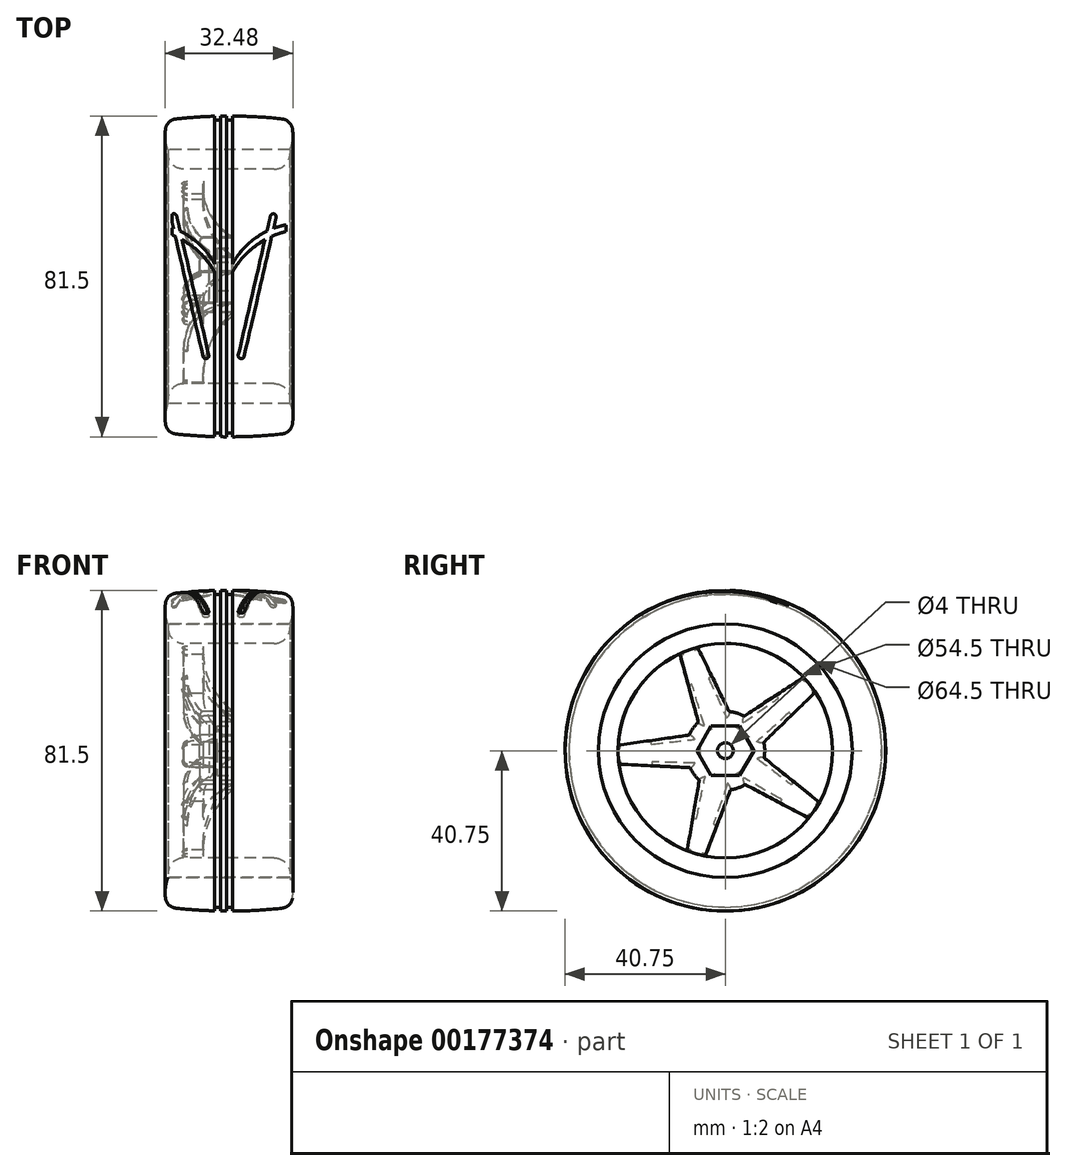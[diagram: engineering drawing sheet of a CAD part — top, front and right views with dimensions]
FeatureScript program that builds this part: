
annotation { "Feature Type Name" : "Feature", "Feature Type Description" : "" }
export const myFeature = defineFeature(function(context is Context, id is Id, definition is map)
    precondition{}
    {
        {
            var Q0;
            Q0=qCreatedBy(makeId("Front.planeOp"),FACE);
            var sketch = newSketch(context, id + "F0", { "sketchPlane" : qUnion([Q0])});
            skLineSegment(sketch, "E0", {"start": v(0, 0) * mm, "end": v(0, 27.25) * mm, "construction": true});
            skLineSegment(sketch, "E1", {"start": v(0, 27.25) * mm, "end": v(18.55, 27.25) * mm, "construction": true});
            skLineSegment(sketch, "E2", {"start": v(18.55, 27.25) * mm, "end": v(18.55, 32.25) * mm, "construction": true});
            skLineSegment(sketch, "E3", {"start": v(18.55, 32.25) * mm, "end": v(-12.45, 32.25) * mm, "construction": true});
            skLineSegment(sketch, "E4", {"start": v(-12.45, 32.25) * mm, "end": v(-12.45, 27.25) * mm, "construction": true});
            skLineSegment(sketch, "E5", {"start": v(-12.45, 27.25) * mm, "end": v(-1.95, 27.25) * mm, "construction": true});
            skLineSegment(sketch, "E6", {"start": v(-1.95, 27.25) * mm, "end": v(-1.95, 0) * mm, "construction": true});
            skLineSegment(sketch, "E7", {"start": v(-1.95, 0) * mm, "end": v(0, 0) * mm, "construction": true});
            skSolve(sketch);
        }
        {
            var Q0;
            Q0=qCreatedBy(makeId("Front.planeOp"),FACE);
            var sketch = newSketch(context, id + "F1", { "sketchPlane" : qUnion([Q0])});
            skLineSegment(sketch, "E8", {"start": v(-20, 0) * mm, "end": v(20, 0) * mm, "construction": true});
            skLineSegment(sketch, "E9", {"start": v(-1.95, 2) * mm, "end": v(0, 2) * mm});
            skLineSegment(sketch, "E10", {"start": v(0, 2) * mm, "end": v(0, 6.5) * mm, "construction": true});
            skLineSegment(sketch, "E11", {"start": v(0, 6.5) * mm, "end": v(-1.95, 6.5) * mm, "construction": true});
            skLineSegment(sketch, "E12", {"start": v(-1.95, 6.5) * mm, "end": v(-1.95, 2) * mm});
            skLineSegment(sketch, "E13", {"start": v(-8.45, 27.25) * mm, "end": v(-8.45, 18.86) * mm});
            skArc(sketch, "E14", {"start": v(-8.45, 18.86) * mm, "mid": v(-6.73, 11.88) * mm, "end": v(-1.95, 6.5) * mm});
            skArc(sketch, "E15", {"start": v(-12.45, 31.25) * mm, "mid": v(-11.28, 28.42) * mm, "end": v(-8.45, 27.25) * mm});
            skLineSegment(sketch, "E16", {"start": v(-12.45, 31.25) * mm, "end": v(-12.45, 32.25) * mm});
            skLineSegment(sketch, "E17", {"start": v(-12.45, 32.25) * mm, "end": v(18.55, 32.25) * mm});
            skLineSegment(sketch, "E18", {"start": v(18.55, 32.25) * mm, "end": v(18.55, 31.25) * mm});
            skLineSegment(sketch, "E19", {"start": v(14.55, 27.25) * mm, "end": v(-3.45, 27.25) * mm});
            skArc(sketch, "E20", {"start": v(-3.45, 27.25) * mm, "mid": v(-1.97, 17.9) * mm, "end": v(3.64, 10.3) * mm});
            skPoint(sketch, "E21.visualSharp", {"position": v(18.55, 27.25) * mm});
            skArc(sketch, "E21.filletArc", {"start": v(14.55, 27.25) * mm, "mid": v(17.38, 28.42) * mm, "end": v(18.55, 31.25) * mm});
            skLineSegment(sketch, "E22", {"start": v(4, 9.53) * mm, "end": v(4, 3) * mm});
            skLineSegment(sketch, "E23", {"start": v(4, 3) * mm, "end": v(0, 3) * mm});
            skLineSegment(sketch, "E24", {"start": v(0, 3) * mm, "end": v(0, 2) * mm});
            skPoint(sketch, "E25.visualSharp", {"position": v(4, 10) * mm});
            skArc(sketch, "E25.filletArc", {"start": v(4, 9.53) * mm, "mid": v(3.9, 9.95) * mm, "end": v(3.64, 10.3) * mm});
            skSolve(sketch);
        }
        {
            var Q0;
            Q0 = qSketchRegion(id + "F1", true);
            var Q1;
            Q1=sQuery(id+"F1.wireOp",EDGE,"E8");
            revolve(context, id + "F2", {"surfaceOperationType" : NewSurfaceOperationType.NEW, "entities" : qUnion([Q0]), "axis" : qUnion([Q1]), "revolveType" : RevolveType.FULL});
        }
        {
            var Q0;
            Q0=makeQuery(id+"F2.opRevolve","SWEPT_FACE",FACE,{"disambiguationData":[OSD([sQuery(id+"F1.wireOp",EDGE,"E22")])]});
            var sketch = newSketch(context, id + "F3", { "sketchPlane" : qUnion([Q0])});
            skCircle(sketch, "E26.cCircle", {"center": v(0, 0) * mm, "radius": 6.25 * mm, "construction": true});
            skLineSegment(sketch, "E26.0", {"start": v(-3.6, 6.25) * mm, "end": v(3.6, 6.25) * mm});
            skLineSegment(sketch, "E26.1", {"start": v(3.6, 6.25) * mm, "end": v(7.22, 0) * mm});
            skLineSegment(sketch, "E26.2", {"start": v(7.22, 0) * mm, "end": v(3.6, -6.25) * mm});
            skLineSegment(sketch, "E26.3", {"start": v(3.6, -6.25) * mm, "end": v(-3.6, -6.25) * mm});
            skLineSegment(sketch, "E26.4", {"start": v(-3.6, -6.25) * mm, "end": v(-7.22, 0) * mm});
            skLineSegment(sketch, "E26.5", {"start": v(-7.22, 0) * mm, "end": v(-3.6, 6.25) * mm});
            skPoint(sketch, "E26.0.midPoint", {"position": v(0, 6.25) * mm});
            skSolve(sketch);
        }
        {
            var Q0;
            Q0 = qSketchRegion(id + "F3", true);
            var Q1;
            Q1=makeQuery(id+"F2.opRevolve","SWEPT_FACE",FACE,{"disambiguationData":[OSD([sQuery(id+"F1.wireOp",EDGE,"E24")])]});
            extrude(context, id + "F4", {"entities" : qUnion([Q0]), "operationType" : NewBodyOperationType.REMOVE, "endBound" : BoundingType.UP_TO_SURFACE, "oppositeDirection" : true, "depth" : 25 * mm, "endBoundEntityFace" : qUnion([Q1]), "offsetDistance" : 25 * mm});
        }
        {
            var Q0;
            Q0=makeQuery(id+"F2.opRevolve","SWEPT_FACE",FACE,{"disambiguationData":[OSD([sQuery(id+"F1.wireOp",EDGE,"E16")])]});
            var sketch = newSketch(context, id + "F5", { "sketchPlane" : qUnion([Q0])});
            skLineSegment(sketch, "E27", {"start": v(11.62, 24.65) * mm, "end": v(6.88, 7.26) * mm});
            skArc(sketch, "E28", {"start": v(9.17, 3.98) * mm, "mid": v(8.2, 5.74) * mm, "end": v(6.88, 7.26) * mm});
            skLineSegment(sketch, "E29", {"start": v(9.17, 3.98) * mm, "end": v(27.21, 1.4) * mm});
            skArc(sketch, "E30", {"start": v(27.21, 1.4) * mm, "mid": v(22.63, 15.18) * mm, "end": v(11.62, 24.65) * mm});
            skLineSegment(sketch, "E31", {"start": v(0, 0) * mm, "end": v(22.32, 15.63) * mm, "construction": true});
            skLineSegment(sketch, "E32.1.0", {"start": v(-19.85, 18.66) * mm, "end": v(-4.78, 8.79) * mm});
            skArc(sketch, "E32.1.1", {"start": v(7.08, 26.31) * mm, "mid": v(-7.44, 26.21) * mm, "end": v(-19.85, 18.66) * mm});
            skLineSegment(sketch, "E32.1.2", {"start": v(-0.95, 9.95) * mm, "end": v(7.08, 26.31) * mm});
            skArc(sketch, "E32.1.3", {"start": v(-0.95, 9.95) * mm, "mid": v(-2.92, 9.56) * mm, "end": v(-4.78, 8.79) * mm});
            skLineSegment(sketch, "E32.2.0", {"start": v(-23.89, -13.12) * mm, "end": v(-9.83, -1.83) * mm});
            skArc(sketch, "E32.2.1", {"start": v(-22.84, 14.87) * mm, "mid": v(-27.23, 1.02) * mm, "end": v(-23.89, -13.12) * mm});
            skLineSegment(sketch, "E32.2.2", {"start": v(-9.76, 2.17) * mm, "end": v(-22.84, 14.87) * mm});
            skArc(sketch, "E32.2.3", {"start": v(-9.76, 2.17) * mm, "mid": v(-10, 0.17) * mm, "end": v(-9.83, -1.83) * mm});
            skLineSegment(sketch, "E32.3.0", {"start": v(5.1, -26.77) * mm, "end": v(-1.3, -9.92) * mm});
            skArc(sketch, "E32.3.1", {"start": v(-21.2, -17.13) * mm, "mid": v(-9.38, -25.58) * mm, "end": v(5.1, -26.77) * mm});
            skLineSegment(sketch, "E32.3.2", {"start": v(-5.08, -8.61) * mm, "end": v(-21.2, -17.13) * mm});
            skArc(sketch, "E32.3.3", {"start": v(-5.08, -8.61) * mm, "mid": v(-3.26, -9.46) * mm, "end": v(-1.3, -9.92) * mm});
            skLineSegment(sketch, "E32.4.0", {"start": v(27.03, -3.43) * mm, "end": v(9.03, -4.3) * mm});
            skArc(sketch, "E32.4.1", {"start": v(9.74, -25.45) * mm, "mid": v(21.43, -16.83) * mm, "end": v(27.03, -3.43) * mm});
            skLineSegment(sketch, "E32.4.2", {"start": v(6.62, -7.5) * mm, "end": v(9.74, -25.45) * mm});
            skArc(sketch, "E32.4.3", {"start": v(6.62, -7.5) * mm, "mid": v(7.99, -6.02) * mm, "end": v(9.03, -4.3) * mm});
            skSolve(sketch);
        }
        {
            var Q0;
            Q0 = qSketchRegion(id + "F5", true);
            extrude(context, id + "F6", {"entities" : qUnion([Q0]), "operationType" : NewBodyOperationType.REMOVE, "endBound" : BoundingType.THROUGH_ALL, "oppositeDirection" : true, "depth" : 25 * mm, "offsetDistance" : 25 * mm});
        }
        {
            var Q0;
            Q0=makeQuery(id+"F6.boolean.opBoolean","INTERSECT",EDGE,{"derivedFrom":[makeQuery(id+"F2.opRevolve","SWEPT_FACE",FACE,{"disambiguationData":[OSD([sQuery(id+"F1.wireOp",EDGE,"E14")])]}),makeQuery(id+"F6.opExtrude","SWEPT_FACE",FACE,{"disambiguationData":[OSD([sQuery(id+"F5.wireOp",EDGE,"E32.2.0")])]})]});
            var Q1;
            Q1=makeQuery(id+"F6.boolean.opBoolean","INTERSECT",EDGE,{"derivedFrom":[makeQuery(id+"F2.opRevolve","SWEPT_FACE",FACE,{"disambiguationData":[OSD([sQuery(id+"F1.wireOp",EDGE,"E13")])]}),makeQuery(id+"F6.opExtrude","SWEPT_FACE",FACE,{"disambiguationData":[OSD([sQuery(id+"F5.wireOp",EDGE,"E32.3.2")])]})]});
            var Q2;
            Q2=makeQuery(id+"F6.boolean.opBoolean","INTERSECT",EDGE,{"derivedFrom":[makeQuery(id+"F2.opRevolve","SWEPT_FACE",FACE,{"disambiguationData":[OSD([sQuery(id+"F1.wireOp",EDGE,"E14")])]}),makeQuery(id+"F6.opExtrude","SWEPT_FACE",FACE,{"disambiguationData":[OSD([sQuery(id+"F5.wireOp",EDGE,"E32.3.3")])]})]});
            var Q3;
            Q3=makeQuery(id+"F6.boolean.opBoolean","INTERSECT",EDGE,{"derivedFrom":[makeQuery(id+"F2.opRevolve","SWEPT_FACE",FACE,{"disambiguationData":[OSD([sQuery(id+"F1.wireOp",EDGE,"E14")])]}),makeQuery(id+"F6.opExtrude","SWEPT_FACE",FACE,{"disambiguationData":[OSD([sQuery(id+"F5.wireOp",EDGE,"E32.2.3")])]})]});
            var Q4;
            Q4=makeQuery(id+"F6.boolean.opBoolean","INTERSECT",EDGE,{"derivedFrom":[makeQuery(id+"F2.opRevolve","SWEPT_FACE",FACE,{"disambiguationData":[OSD([sQuery(id+"F1.wireOp",EDGE,"E14")])]}),makeQuery(id+"F6.opExtrude","SWEPT_FACE",FACE,{"disambiguationData":[OSD([sQuery(id+"F5.wireOp",EDGE,"E32.2.2")])]})]});
            var Q5;
            Q5=makeQuery(id+"F6.boolean.opBoolean","INTERSECT",EDGE,{"derivedFrom":[makeQuery(id+"F2.opRevolve","SWEPT_FACE",FACE,{"disambiguationData":[OSD([sQuery(id+"F1.wireOp",EDGE,"E14")])]}),makeQuery(id+"F6.opExtrude","SWEPT_FACE",FACE,{"disambiguationData":[OSD([sQuery(id+"F5.wireOp",EDGE,"E32.1.3")])]})]});
            var Q6;
            Q6=makeQuery(id+"F6.boolean.opBoolean","INTERSECT",EDGE,{"derivedFrom":[makeQuery(id+"F2.opRevolve","SWEPT_FACE",FACE,{"disambiguationData":[OSD([sQuery(id+"F1.wireOp",EDGE,"E14")])]}),makeQuery(id+"F6.opExtrude","SWEPT_FACE",FACE,{"disambiguationData":[OSD([sQuery(id+"F5.wireOp",EDGE,"E32.1.0")])]})]});
            var Q7;
            Q7=makeQuery(id+"F6.boolean.opBoolean","INTERSECT",EDGE,{"derivedFrom":[makeQuery(id+"F2.opRevolve","SWEPT_FACE",FACE,{"disambiguationData":[OSD([sQuery(id+"F1.wireOp",EDGE,"E14")])]}),makeQuery(id+"F6.opExtrude","SWEPT_FACE",FACE,{"disambiguationData":[OSD([sQuery(id+"F5.wireOp",EDGE,"E32.3.0")])]})]});
            var Q8;
            Q8=makeQuery(id+"F6.boolean.opBoolean","INTERSECT",EDGE,{"derivedFrom":[makeQuery(id+"F2.opRevolve","SWEPT_FACE",FACE,{"disambiguationData":[OSD([sQuery(id+"F1.wireOp",EDGE,"E14")])]}),makeQuery(id+"F6.opExtrude","SWEPT_FACE",FACE,{"disambiguationData":[OSD([sQuery(id+"F5.wireOp",EDGE,"E32.4.2")])]})]});
            var Q9;
            Q9=makeQuery(id+"F6.boolean.opBoolean","INTERSECT",EDGE,{"derivedFrom":[makeQuery(id+"F2.opRevolve","SWEPT_FACE",FACE,{"disambiguationData":[OSD([sQuery(id+"F1.wireOp",EDGE,"E14")])]}),makeQuery(id+"F6.opExtrude","SWEPT_FACE",FACE,{"disambiguationData":[OSD([sQuery(id+"F5.wireOp",EDGE,"E32.4.3")])]})]});
            var Q10;
            Q10=makeQuery(id+"F6.boolean.opBoolean","INTERSECT",EDGE,{"derivedFrom":[makeQuery(id+"F2.opRevolve","SWEPT_FACE",FACE,{"disambiguationData":[OSD([sQuery(id+"F1.wireOp",EDGE,"E14")])]}),makeQuery(id+"F6.opExtrude","SWEPT_FACE",FACE,{"disambiguationData":[OSD([sQuery(id+"F5.wireOp",EDGE,"E32.4.0")])]})]});
            var Q11;
            Q11=makeQuery(id+"F6.boolean.opBoolean","INTERSECT",EDGE,{"derivedFrom":[makeQuery(id+"F2.opRevolve","SWEPT_FACE",FACE,{"disambiguationData":[OSD([sQuery(id+"F1.wireOp",EDGE,"E14")])]}),makeQuery(id+"F6.opExtrude","SWEPT_FACE",FACE,{"disambiguationData":[OSD([sQuery(id+"F5.wireOp",EDGE,"E29")])]})]});
            var Q12;
            Q12=makeQuery(id+"F6.boolean.opBoolean","INTERSECT",EDGE,{"derivedFrom":[makeQuery(id+"F2.opRevolve","SWEPT_FACE",FACE,{"disambiguationData":[OSD([sQuery(id+"F1.wireOp",EDGE,"E14")])]}),makeQuery(id+"F6.opExtrude","SWEPT_FACE",FACE,{"disambiguationData":[OSD([sQuery(id+"F5.wireOp",EDGE,"E28")])]})]});
            var Q13;
            Q13=makeQuery(id+"F6.boolean.opBoolean","INTERSECT",EDGE,{"derivedFrom":[makeQuery(id+"F2.opRevolve","SWEPT_FACE",FACE,{"disambiguationData":[OSD([sQuery(id+"F1.wireOp",EDGE,"E14")])]}),makeQuery(id+"F6.opExtrude","SWEPT_FACE",FACE,{"disambiguationData":[OSD([sQuery(id+"F5.wireOp",EDGE,"E27")])]})]});
            var Q14;
            Q14=makeQuery(id+"F6.boolean.opBoolean","INTERSECT",EDGE,{"derivedFrom":[makeQuery(id+"F2.opRevolve","SWEPT_FACE",FACE,{"disambiguationData":[OSD([sQuery(id+"F1.wireOp",EDGE,"E14")])]}),makeQuery(id+"F6.opExtrude","SWEPT_FACE",FACE,{"disambiguationData":[OSD([sQuery(id+"F5.wireOp",EDGE,"E32.1.2")])]})]});
            fillet(context, id + "F7", {"entities" : qUnion([Q0, Q1, Q2, Q3, Q4, Q5, Q6, Q7, Q8, Q9, Q10, Q11, Q12, Q13, Q14]), "radius" : 1 * mm, "tangentPropagation" : true, "allowEdgeOverflow" : false});
        }
        {
            var Q0;
            Q0=makeQuery(id+"F6.boolean.opBoolean","COPY",EDGE,{"derivedFrom":makeQuery(id+"F6.opExtrude","SWEPT_EDGE",EDGE,{"disambiguationData":[OSD([sQuery(id+"F5.wireOp",EDGE,"E32.2.1"),sQuery(id+"F5.wireOp",EDGE,"E32.2.2")])]})});
            var Q1;
            Q1=makeQuery(id+"F6.boolean.opBoolean","COPY",EDGE,{"derivedFrom":makeQuery(id+"F6.opExtrude","SWEPT_EDGE",EDGE,{"disambiguationData":[OSD([sQuery(id+"F5.wireOp",EDGE,"E27"),sQuery(id+"F5.wireOp",EDGE,"E30")])]})});
            var Q2;
            Q2=makeQuery(id+"F6.boolean.opBoolean","COPY",EDGE,{"derivedFrom":makeQuery(id+"F6.opExtrude","SWEPT_EDGE",EDGE,{"disambiguationData":[OSD([sQuery(id+"F5.wireOp",EDGE,"E32.4.0"),sQuery(id+"F5.wireOp",EDGE,"E32.4.1")])]})});
            var Q3;
            Q3=makeQuery(id+"F6.boolean.opBoolean","COPY",EDGE,{"derivedFrom":makeQuery(id+"F6.opExtrude","SWEPT_EDGE",EDGE,{"disambiguationData":[OSD([sQuery(id+"F5.wireOp",EDGE,"E32.4.1"),sQuery(id+"F5.wireOp",EDGE,"E32.4.2")])]})});
            var Q4;
            Q4=makeQuery(id+"F6.boolean.opBoolean","COPY",EDGE,{"derivedFrom":makeQuery(id+"F6.opExtrude","SWEPT_EDGE",EDGE,{"disambiguationData":[OSD([sQuery(id+"F5.wireOp",EDGE,"E32.2.0"),sQuery(id+"F5.wireOp",EDGE,"E32.2.1")])]})});
            fillet(context, id + "F8", {"entities" : qUnion([Q0, Q1, Q2, Q3, Q4]), "radius" : 0.5 * mm, "tangentPropagation" : true, "allowEdgeOverflow" : false});
        }
        {
            var Q0;
            Q0=qCreatedBy(makeId("Front.planeOp"),FACE);
            var sketch = newSketch(context, id + "F9", { "sketchPlane" : qUnion([Q0])});
            skLineSegment(sketch, "E33", {"start": v(39.81, 0) * mm, "end": v(-23.66, 0) * mm, "construction": true});
            skArc(sketch, "E34", {"start": v(16.54, 40.02) * mm, "mid": v(3.05, 40.75) * mm, "end": v(-10.44, 40.02) * mm});
            skArc(sketch, "E35", {"start": v(-13.08, 37.48) * mm, "mid": v(-13.11, 34.82) * mm, "end": v(-12.45, 32.25) * mm});
            skArc(sketch, "E36", {"start": v(18.55, 32.25) * mm, "mid": v(19.21, 34.82) * mm, "end": v(19.18, 37.48) * mm});
            skLineSegment(sketch, "E37", {"start": v(18.55, 32.25) * mm, "end": v(-12.45, 32.25) * mm});
            skPoint(sketch, "E38.visualSharp", {"position": v(18.55, 39.79) * mm});
            skArc(sketch, "E38.filletArc", {"start": v(19.18, 37.48) * mm, "mid": v(18.3, 39.2) * mm, "end": v(16.54, 40.02) * mm});
            skPoint(sketch, "E39.visualSharp", {"position": v(-12.45, 39.79) * mm});
            skArc(sketch, "E39.filletArc", {"start": v(-10.44, 40.02) * mm, "mid": v(-12.2, 39.2) * mm, "end": v(-13.08, 37.48) * mm});
            skSolve(sketch);
        }
        {
            var Q0;
            Q0 = qSketchRegion(id + "F9", true);
            var Q1;
            Q1=sQuery(id+"F9.wireOp",EDGE,"E33");
            revolve(context, id + "F10", {"surfaceOperationType" : NewSurfaceOperationType.NEW, "entities" : qUnion([Q0]), "axis" : qUnion([Q1]), "revolveType" : RevolveType.FULL});
        }
        {
            var Q0;
            Q0=qCreatedBy(makeId("Front.planeOp"),FACE);
            var sketch = newSketch(context, id + "F11", { "sketchPlane" : qUnion([Q0])});
            skLineSegment(sketch, "E40", {"start": v(0.92, 41.75) * mm, "end": v(0.92, 39.75) * mm});
            skLineSegment(sketch, "E41", {"start": v(-0.58, 39.75) * mm, "end": v(-0.58, 41.75) * mm});
            skLineSegment(sketch, "E42", {"start": v(-0.58, 41.75) * mm, "end": v(0.92, 41.75) * mm});
            skLineSegment(sketch, "E43", {"start": v(3.92, 41.75) * mm, "end": v(3.92, 39.75) * mm});
            skLineSegment(sketch, "E44", {"start": v(2.42, 39.75) * mm, "end": v(2.42, 41.75) * mm});
            skLineSegment(sketch, "E45", {"start": v(2.42, 41.75) * mm, "end": v(3.92, 41.75) * mm});
            skLineSegment(sketch, "E46", {"start": v(3.92, 39.75) * mm, "end": v(2.42, 39.75) * mm});
            skLineSegment(sketch, "E47", {"start": v(0.92, 39.75) * mm, "end": v(-0.58, 39.75) * mm});
            skLineSegment(sketch, "E48", {"start": v(0, 0) * mm, "end": v(-18.32, 0) * mm, "construction": true});
            skSolve(sketch);
        }
        {
            var Q0;
            Q0 = qSketchRegion(id + "F11", true);
            var Q1;
            Q1=makeQuery(id+"F10.opRevolve","SWEPT_FACE",FACE,{"disambiguationData":[OSD([sQuery(id+"F9.wireOp",EDGE,"E34")])]});
            revolve(context, id + "F12", {"operationType" : NewBodyOperationType.REMOVE, "surfaceOperationType" : NewSurfaceOperationType.NEW, "entities" : qUnion([Q0]), "axis" : qUnion([Q1]), "revolveType" : RevolveType.FULL, "oppositeDirection" : true});
        }
        {
            var Q0;
            Q0=qCreatedBy(makeId("Top.planeOp"),FACE);
            cPlane(context, id + "F13", {"entities" : qUnion([Q0]), "cplaneType" : CPlaneType.OFFSET, "offset" : 42.75 * mm, "width" : 150 * mm, "height" : 150 * mm});
        }
        {
            var Q0;
            Q0=qCreatedBy(id+"F13.planeOp",FACE);
            var sketch = newSketch(context, id + "F14", { "sketchPlane" : qUnion([Q0])});
            skLineSegment(sketch, "E49", {"start": v(0, 0) * mm, "end": v(0, 2) * mm});
            skArc(sketch, "E50", {"start": v(0, 2) * mm, "mid": v(-7.37, 10.38) * mm, "end": v(-18.08, 13.5) * mm});
            skArc(sketch, "E51", {"start": v(0, 0) * mm, "mid": v(-7.42, 8.45) * mm, "end": v(-18.08, 12) * mm});
            skLineSegment(sketch, "E52", {"start": v(-18.08, 12) * mm, "end": v(-18.08, 13.5) * mm});
            skLineSegment(sketch, "E53", {"start": v(1.67, 6.52) * mm, "end": v(1.67, -6.35) * mm, "construction": true});
            skArc(sketch, "E54.MirrorCS", {"start": v(3.34, 0) * mm, "mid": v(10.75, 8.45) * mm, "end": v(21.42, 12) * mm});
            skArc(sketch, "E55.MirrorCS", {"start": v(3.34, 2) * mm, "mid": v(10.7, 10.38) * mm, "end": v(21.42, 13.5) * mm});
            skLineSegment(sketch, "E56.MirrorCS", {"start": v(21.42, 12) * mm, "end": v(21.42, 13.5) * mm});
            skLineSegment(sketch, "E57.MirrorCS", {"start": v(3.34, 0) * mm, "end": v(3.34, 2) * mm});
            skSolve(sketch);
        }
        {
            var Q0;
            Q0 = qSketchRegion(id + "F14", true);
            var Q1;
            Q1=makeQuery(id+"F12.boolean.opBoolean","COPY",FACE,{"derivedFrom":makeQuery(id+"F12.opRevolve","SWEPT_FACE",FACE,{"disambiguationData":[OSD([sQuery(id+"F11.wireOp",EDGE,"E46")])]})});
            extrude(context, id + "F15", {"entities" : qUnion([Q0]), "operationType" : NewBodyOperationType.REMOVE, "endBound" : BoundingType.UP_TO_SURFACE, "oppositeDirection" : true, "depth" : 25 * mm, "endBoundEntityFace" : qUnion([Q1]), "offsetDistance" : 25 * mm});
        }
        {
            var Q0;
            Q0=qCreatedBy(id+"F13.planeOp",FACE);
            var sketch = newSketch(context, id + "F16", { "sketchPlane" : qUnion([Q0])});
            skLineSegment(sketch, "E58", {"start": v(5.42, -20) * mm, "end": v(13.57, 15.34) * mm});
            skLineSegment(sketch, "E59", {"start": v(13.57, 15.34) * mm, "end": v(15.04, 15) * mm, "construction": true});
            skLineSegment(sketch, "E60", {"start": v(15.04, 15) * mm, "end": v(6.88, -20.34) * mm});
            skLineSegment(sketch, "E61", {"start": v(6.88, -20.34) * mm, "end": v(5.42, -20) * mm, "construction": true});
            skArc(sketch, "E62", {"start": v(15.04, 15) * mm, "mid": v(14.47, 15.9) * mm, "end": v(13.57, 15.34) * mm});
            skArc(sketch, "E63", {"start": v(5.42, -20) * mm, "mid": v(5.98, -20.9) * mm, "end": v(6.88, -20.34) * mm});
            skLineSegment(sketch, "E64", {"start": v(1.67, 11.65) * mm, "end": v(1.67, -13.65) * mm, "construction": true});
            skLineSegment(sketch, "E65.MirrorCS", {"start": v(-2.08, -20) * mm, "end": v(-10.23, 15.34) * mm});
            skLineSegment(sketch, "E66.MirrorCS", {"start": v(-11.7, 15) * mm, "end": v(-3.54, -20.34) * mm});
            skArc(sketch, "E67.MirrorCS", {"start": v(-11.7, 15) * mm, "mid": v(-11.13, 15.9) * mm, "end": v(-10.23, 15.34) * mm});
            skArc(sketch, "E68.MirrorCS", {"start": v(-2.08, -20) * mm, "mid": v(-2.64, -20.9) * mm, "end": v(-3.54, -20.34) * mm});
            skSolve(sketch);
        }
        {
            var Q0;
            Q0=makeQuery(id+"F16.imprint","IMPRINT",FACE,{"disambiguationData":[TD([[makeQuery(id+"F16.imprint","IMPRINT",EDGE,{"derivedFrom":sQuery(id+"F16.wireOp",EDGE,"E58")}),-1.0]])]});
            var Q1;
            Q1=makeQuery(id+"F16.imprint","IMPRINT",FACE,{"disambiguationData":[TD([[makeQuery(id+"F16.imprint","IMPRINT",EDGE,{"derivedFrom":sQuery(id+"F16.wireOp",EDGE,"E65.MirrorCS")}),1.0]])]});
            var Q2;
            {var subQ0=sQuery(id+"F14.wireOp",EDGE,"E57.MirrorCS");var subQ1=sQuery(id+"F14.wireOp",EDGE,"E56.MirrorCS");var subQ2=sQuery(id+"F14.wireOp",EDGE,"E55.MirrorCS");var subQ3=sQuery(id+"F14.wireOp",EDGE,"E54.MirrorCS");Q2=makeQuery(id+"FRkk9yGD8DPVHCN_2.23.F15.boolean.opBoolean","MERGE",FACE,{"derivedFrom":[makeQuery(id+"FRkk9yGD8DPVHCN_2.22.F15.boolean.opBoolean","MERGE",FACE,{"derivedFrom":[makeQuery(id+"FRkk9yGD8DPVHCN_2.21.F15.boolean.opBoolean","MERGE",FACE,{"derivedFrom":[makeQuery(id+"FRkk9yGD8DPVHCN_2.20.F15.boolean.opBoolean","MERGE",FACE,{"derivedFrom":[makeQuery(id+"FRkk9yGD8DPVHCN_2.19.F15.boolean.opBoolean","MERGE",FACE,{"derivedFrom":[makeQuery(id+"FRkk9yGD8DPVHCN_2.18.F15.boolean.opBoolean","MERGE",FACE,{"derivedFrom":[makeQuery(id+"FRkk9yGD8DPVHCN_2.17.F15.boolean.opBoolean","MERGE",FACE,{"derivedFrom":[makeQuery(id+"FRkk9yGD8DPVHCN_2.16.F15.boolean.opBoolean","MERGE",FACE,{"derivedFrom":[makeQuery(id+"FRkk9yGD8DPVHCN_2.15.F15.boolean.opBoolean","MERGE",FACE,{"derivedFrom":[makeQuery(id+"FRkk9yGD8DPVHCN_2.14.F15.boolean.opBoolean","MERGE",FACE,{"derivedFrom":[makeQuery(id+"FRkk9yGD8DPVHCN_2.13.F15.boolean.opBoolean","MERGE",FACE,{"derivedFrom":[makeQuery(id+"FRkk9yGD8DPVHCN_2.12.F15.boolean.opBoolean","MERGE",FACE,{"derivedFrom":[makeQuery(id+"FRkk9yGD8DPVHCN_2.11.F15.boolean.opBoolean","MERGE",FACE,{"derivedFrom":[makeQuery(id+"FRkk9yGD8DPVHCN_2.10.F15.boolean.opBoolean","MERGE",FACE,{"derivedFrom":[makeQuery(id+"FRkk9yGD8DPVHCN_2.9.F15.boolean.opBoolean","MERGE",FACE,{"derivedFrom":[makeQuery(id+"FRkk9yGD8DPVHCN_2.8.F15.boolean.opBoolean","MERGE",FACE,{"derivedFrom":[makeQuery(id+"FRkk9yGD8DPVHCN_2.7.F15.boolean.opBoolean","MERGE",FACE,{"derivedFrom":[makeQuery(id+"FRkk9yGD8DPVHCN_2.6.F15.boolean.opBoolean","MERGE",FACE,{"derivedFrom":[makeQuery(id+"FRkk9yGD8DPVHCN_2.5.F15.boolean.opBoolean","MERGE",FACE,{"derivedFrom":[makeQuery(id+"FRkk9yGD8DPVHCN_2.4.F15.boolean.opBoolean","MERGE",FACE,{"derivedFrom":[makeQuery(id+"FRkk9yGD8DPVHCN_2.3.F15.boolean.opBoolean","MERGE",FACE,{"derivedFrom":[makeQuery(id+"FRkk9yGD8DPVHCN_2.2.F15.boolean.opBoolean","MERGE",FACE,{"derivedFrom":[makeQuery(id+"FRkk9yGD8DPVHCN_2.1.F15.boolean.opBoolean","MERGE",FACE,{"derivedFrom":[makeQuery(id+"F15.boolean.opBoolean","MERGE",FACE,{"derivedFrom":[makeQuery(id+"F12.boolean.opBoolean","COPY",FACE,{"derivedFrom":makeQuery(id+"F12.opRevolve","SWEPT_FACE",FACE,{"disambiguationData":[OSD([sQuery(id+"F11.wireOp",EDGE,"E46")])]})})],"fromTools":[makeQuery(id+"F15.opExtrude","CAP_FACE",FACE,{"disambiguationData":[OSD([subQ3,subQ2,subQ1,subQ0])],"isStart":false})]})],"fromTools":[makeQuery(id+"FRkk9yGD8DPVHCN_2.1.F15.opExtrude","CAP_FACE",FACE,{"disambiguationData":[OSD([subQ3,subQ2,subQ1,subQ0])],"isStart":false})]})],"fromTools":[makeQuery(id+"FRkk9yGD8DPVHCN_2.2.F15.opExtrude","CAP_FACE",FACE,{"disambiguationData":[OSD([subQ3,subQ2,subQ1,subQ0])],"isStart":false})]})],"fromTools":[makeQuery(id+"FRkk9yGD8DPVHCN_2.3.F15.opExtrude","CAP_FACE",FACE,{"disambiguationData":[OSD([subQ3,subQ2,subQ1,subQ0])],"isStart":false})]})],"fromTools":[makeQuery(id+"FRkk9yGD8DPVHCN_2.4.F15.opExtrude","CAP_FACE",FACE,{"disambiguationData":[OSD([subQ3,subQ2,subQ1,subQ0])],"isStart":false})]})],"fromTools":[makeQuery(id+"FRkk9yGD8DPVHCN_2.5.F15.opExtrude","CAP_FACE",FACE,{"disambiguationData":[OSD([subQ3,subQ2,subQ1,subQ0])],"isStart":false})]})],"fromTools":[makeQuery(id+"FRkk9yGD8DPVHCN_2.6.F15.opExtrude","CAP_FACE",FACE,{"disambiguationData":[OSD([subQ3,subQ2,subQ1,subQ0])],"isStart":false})]})],"fromTools":[makeQuery(id+"FRkk9yGD8DPVHCN_2.7.F15.opExtrude","CAP_FACE",FACE,{"disambiguationData":[OSD([subQ3,subQ2,subQ1,subQ0])],"isStart":false})]})],"fromTools":[makeQuery(id+"FRkk9yGD8DPVHCN_2.8.F15.opExtrude","CAP_FACE",FACE,{"disambiguationData":[OSD([subQ3,subQ2,subQ1,subQ0])],"isStart":false})]})],"fromTools":[makeQuery(id+"FRkk9yGD8DPVHCN_2.9.F15.opExtrude","CAP_FACE",FACE,{"disambiguationData":[OSD([subQ3,subQ2,subQ1,subQ0])],"isStart":false})]})],"fromTools":[makeQuery(id+"FRkk9yGD8DPVHCN_2.10.F15.opExtrude","CAP_FACE",FACE,{"disambiguationData":[OSD([subQ3,subQ2,subQ1,subQ0])],"isStart":false})]})],"fromTools":[makeQuery(id+"FRkk9yGD8DPVHCN_2.11.F15.opExtrude","CAP_FACE",FACE,{"disambiguationData":[OSD([subQ3,subQ2,subQ1,subQ0])],"isStart":false})]})],"fromTools":[makeQuery(id+"FRkk9yGD8DPVHCN_2.12.F15.opExtrude","CAP_FACE",FACE,{"disambiguationData":[OSD([subQ3,subQ2,subQ1,subQ0])],"isStart":false})]})],"fromTools":[makeQuery(id+"FRkk9yGD8DPVHCN_2.13.F15.opExtrude","CAP_FACE",FACE,{"disambiguationData":[OSD([subQ3,subQ2,subQ1,subQ0])],"isStart":false})]})],"fromTools":[makeQuery(id+"FRkk9yGD8DPVHCN_2.14.F15.opExtrude","CAP_FACE",FACE,{"disambiguationData":[OSD([subQ3,subQ2,subQ1,subQ0])],"isStart":false})]})],"fromTools":[makeQuery(id+"FRkk9yGD8DPVHCN_2.15.F15.opExtrude","CAP_FACE",FACE,{"disambiguationData":[OSD([subQ3,subQ2,subQ1,subQ0])],"isStart":false})]})],"fromTools":[makeQuery(id+"FRkk9yGD8DPVHCN_2.16.F15.opExtrude","CAP_FACE",FACE,{"disambiguationData":[OSD([subQ3,subQ2,subQ1,subQ0])],"isStart":false})]})],"fromTools":[makeQuery(id+"FRkk9yGD8DPVHCN_2.17.F15.opExtrude","CAP_FACE",FACE,{"disambiguationData":[OSD([subQ3,subQ2,subQ1,subQ0])],"isStart":false})]})],"fromTools":[makeQuery(id+"FRkk9yGD8DPVHCN_2.18.F15.opExtrude","CAP_FACE",FACE,{"disambiguationData":[OSD([subQ3,subQ2,subQ1,subQ0])],"isStart":false})]})],"fromTools":[makeQuery(id+"FRkk9yGD8DPVHCN_2.19.F15.opExtrude","CAP_FACE",FACE,{"disambiguationData":[OSD([subQ3,subQ2,subQ1,subQ0])],"isStart":false})]})],"fromTools":[makeQuery(id+"FRkk9yGD8DPVHCN_2.20.F15.opExtrude","CAP_FACE",FACE,{"disambiguationData":[OSD([subQ3,subQ2,subQ1,subQ0])],"isStart":false})]})],"fromTools":[makeQuery(id+"FRkk9yGD8DPVHCN_2.21.F15.opExtrude","CAP_FACE",FACE,{"disambiguationData":[OSD([subQ3,subQ2,subQ1,subQ0])],"isStart":false})]})],"fromTools":[makeQuery(id+"FRkk9yGD8DPVHCN_2.22.F15.opExtrude","CAP_FACE",FACE,{"disambiguationData":[OSD([subQ3,subQ2,subQ1,subQ0])],"isStart":false})]})],"fromTools":[makeQuery(id+"FRkk9yGD8DPVHCN_2.23.F15.opExtrude","CAP_FACE",FACE,{"disambiguationData":[OSD([subQ3,subQ2,subQ1,subQ0])],"isStart":false})]});}
            extrude(context, id + "F17", {"entities" : qUnion([Q0, Q1]), "operationType" : NewBodyOperationType.REMOVE, "endBound" : BoundingType.UP_TO_SURFACE, "oppositeDirection" : true, "depth" : 25 * mm, "endBoundEntityFace" : qUnion([Q2]), "offsetDistance" : 25 * mm});
        }
    });
